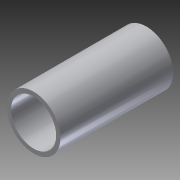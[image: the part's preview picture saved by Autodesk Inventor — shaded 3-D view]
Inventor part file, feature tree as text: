
AUTODESK INVENTOR PART (.ipt)
format: ipt  version: 2014 SP1 (Build 180222100, 222)  size: 84,480 bytes
history: native  units: in
note: dims shown in document units (in); Inventor stores cm internally (conversion verified against a paired STEP export)
features: extrude x1, sketch x1
ambient origin geometry x8: Origin, YZ Plane, XZ Plane, XY Plane, X Axis, Y Axis, Z Axis, Center Point
bodies: Solid1 (feature_tree)
feature tree (2):
  extrude  "Extrusion1"  Depth=5.0in
  sketch  "Sketch1"  dims[d0=2.0in d1=2.375in d2=5.0in d3=0.0in]
